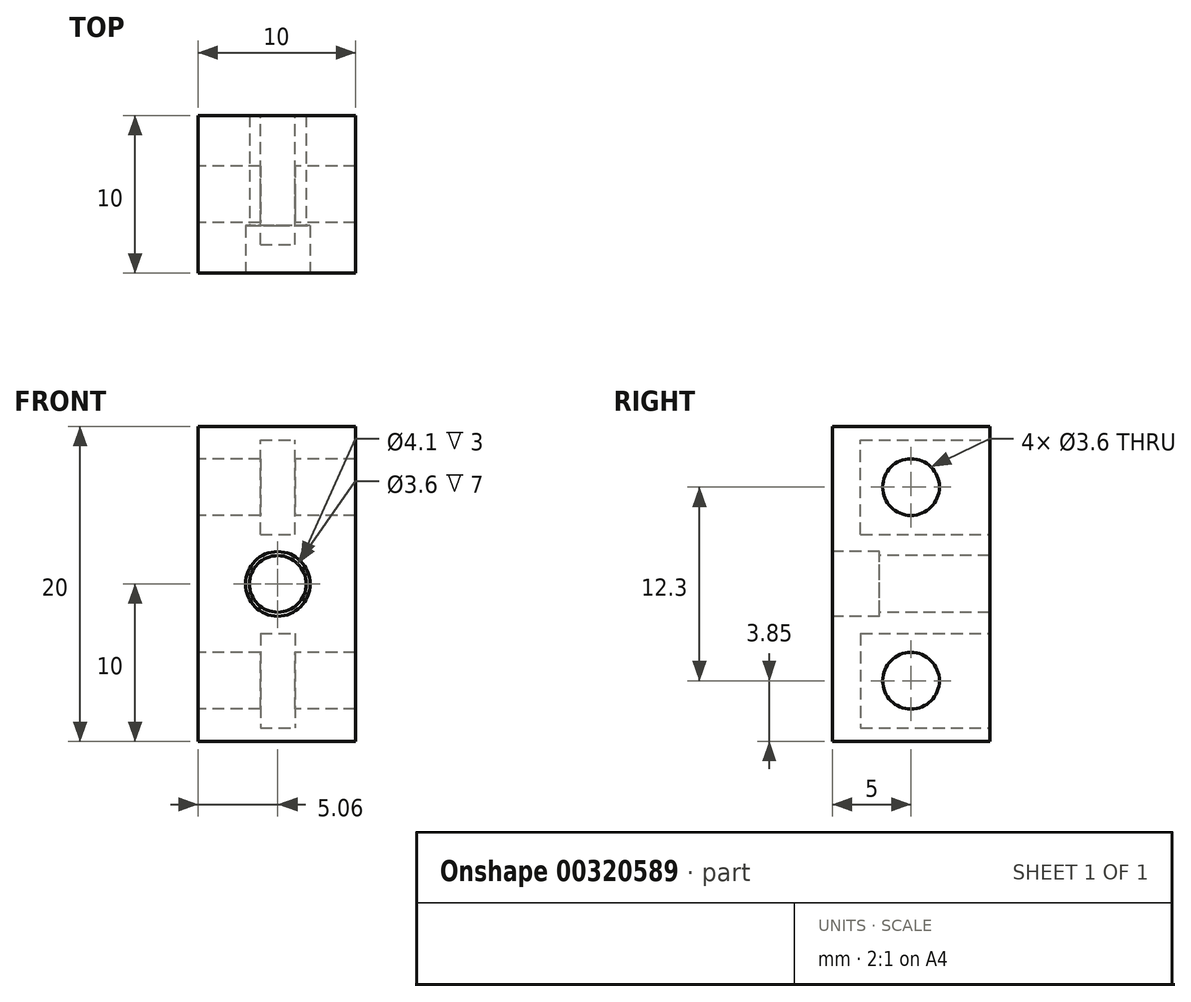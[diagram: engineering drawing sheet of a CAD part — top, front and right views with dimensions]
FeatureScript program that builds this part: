
annotation { "Feature Type Name" : "Feature", "Feature Type Description" : "" }
export const myFeature = defineFeature(function(context is Context, id is Id, definition is map)
    precondition{}
    {
        {
            var Q0;
            Q0=qCreatedBy(makeId("Front.planeOp"),FACE);
            var sketch = newSketch(context, id + "F0", { "sketchPlane" : qUnion([Q0])});
            skLineSegment(sketch, "E0.bottom", {"start": v(-5.06, 10) * mm, "end": v(4.94, 10) * mm});
            skLineSegment(sketch, "E0.top", {"start": v(-5.06, -10) * mm, "end": v(4.94, -10) * mm});
            skLineSegment(sketch, "E0.left", {"start": v(-5.06, 10) * mm, "end": v(-5.06, -10) * mm});
            skLineSegment(sketch, "E0.right", {"start": v(4.94, 10) * mm, "end": v(4.94, -10) * mm});
            skPoint(sketch, "E1", {"position": v(0, 0) * mm});
            skPoint(sketch, "E1.positionSnap0", {"position": v(4.94, 0) * mm});
            skCircle(sketch, "E2", {"center": v(0, 0) * mm, "radius": 3.25 * mm, "construction": true});
            skCircle(sketch, "E3", {"center": v(0, 0) * mm, "radius": 1.8 * mm, "construction": true});
            skLineSegment(sketch, "E4.bottom", {"start": v(-1.1, -3.15) * mm, "end": v(1.1, -3.15) * mm, "construction": true});
            skLineSegment(sketch, "E4.top", {"start": v(-1.1, -9.15) * mm, "end": v(1.1, -9.15) * mm, "construction": true});
            skLineSegment(sketch, "E4.left", {"start": v(-1.1, -3.15) * mm, "end": v(-1.1, -9.15) * mm, "construction": true});
            skLineSegment(sketch, "E4.right", {"start": v(1.1, -3.15) * mm, "end": v(1.1, -9.15) * mm, "construction": true});
            skPoint(sketch, "E5", {"position": v(1.1, -6.15) * mm});
            skPoint(sketch, "E6", {"position": v(0, -9.15) * mm});
            skLineSegment(sketch, "E7.MirrorCS", {"start": v(-1.1, 3.15) * mm, "end": v(-1.1, 9.15) * mm, "construction": true});
            skLineSegment(sketch, "E8.MirrorCS", {"start": v(-1.1, 3.15) * mm, "end": v(1.1, 3.15) * mm, "construction": true});
            skLineSegment(sketch, "E9.MirrorCS", {"start": v(1.1, 3.15) * mm, "end": v(1.1, 9.15) * mm, "construction": true});
            skLineSegment(sketch, "E10.MirrorCS", {"start": v(-1.1, 9.15) * mm, "end": v(1.1, 9.15) * mm, "construction": true});
            skLineSegment(sketch, "E11.MirrorCS", {"start": v(-1.1, 3.15) * mm, "end": v(-1.1, 9.15) * mm});
            skLineSegment(sketch, "E12.MirrorCS", {"start": v(-1.1, 3.15) * mm, "end": v(1.1, 3.15) * mm});
            skPoint(sketch, "E13.orphan", {"position": v(1.1, 2.85) * mm});
            skPoint(sketch, "E14.MirrorCS.start.orphan", {"position": v(1.1, -3.15) * mm});
            skSolve(sketch);
        }
        {
            var Q0;
            Q0=makeQuery(id+"F0.imprint","IMPRINT",FACE,{"disambiguationData":[TD([[makeQuery(id+"F0.imprint","IMPRINT",EDGE,{"derivedFrom":sQuery(id+"F0.wireOp",EDGE,"E0.bottom")}),-1.0]])]});
            extrude(context, id + "F1", {"entities" : qUnion([Q0]), "depth" : 10 * mm});
        }
        {
            var Q0;
            Q0=makeQuery(id+"F1.opExtrude","CAP_FACE",FACE,{"disambiguationData":[OSD([sQuery(id+"F0.wireOp",EDGE,"E0.bottom"),sQuery(id+"F0.wireOp",EDGE,"E0.top"),sQuery(id+"F0.wireOp",EDGE,"E0.left"),sQuery(id+"F0.wireOp",EDGE,"E0.right")])],"isStart":true});
            var sketch = newSketch(context, id + "F2", { "sketchPlane" : qUnion([Q0])});
            skLineSegment(sketch, "E15.0", {"start": v(1.1, 9.15) * mm, "end": v(-1.1, 9.15) * mm});
            skLineSegment(sketch, "E15.1", {"start": v(-1.1, 3.15) * mm, "end": v(-1.1, 9.15) * mm});
            skLineSegment(sketch, "E15.2", {"start": v(1.1, 3.15) * mm, "end": v(1.1, 9.15) * mm});
            skLineSegment(sketch, "E15.3", {"start": v(1.1, 3.15) * mm, "end": v(-1.1, 3.15) * mm});
            skLineSegment(sketch, "E15.4", {"start": v(1.1, -3.15) * mm, "end": v(-1.1, -3.15) * mm});
            skLineSegment(sketch, "E15.5", {"start": v(-1.1, -3.15) * mm, "end": v(-1.1, -9.15) * mm});
            skLineSegment(sketch, "E15.6", {"start": v(1.1, -3.15) * mm, "end": v(1.1, -9.15) * mm});
            skLineSegment(sketch, "E15.7", {"start": v(1.1, -9.15) * mm, "end": v(-1.1, -9.15) * mm});
            skSolve(sketch);
        }
        {
            var Q0;
            Q0 = qSketchRegion(id + "F2", true);
            extrude(context, id + "F3", {"entities" : qUnion([Q0]), "operationType" : NewBodyOperationType.REMOVE, "oppositeDirection" : true, "depth" : 8.2 * mm});
        }
        {
            var Q0;
            Q0=makeQuery(id+"F1.opExtrude","CAP_FACE",FACE,{"disambiguationData":[OSD([sQuery(id+"F0.wireOp",EDGE,"E0.bottom"),sQuery(id+"F0.wireOp",EDGE,"E0.top"),sQuery(id+"F0.wireOp",EDGE,"E0.left"),sQuery(id+"F0.wireOp",EDGE,"E0.right")])],"isStart":false});
            var sketch = newSketch(context, id + "F4", { "sketchPlane" : qUnion([Q0])});
            skCircle(sketch, "E16", {"center": v(0, 0) * mm, "radius": 2.05 * mm});
            skSolve(sketch);
        }
        {
            var Q0;
            Q0=makeQuery(id+"F4.imprint","IMPRINT",FACE,{"disambiguationData":[TD([[makeQuery(id+"F4.imprint","IMPRINT",EDGE,{"derivedFrom":sQuery(id+"F4.wireOp",EDGE,"E16")}),1.0]])]});
            var Q1;
            Q1=sQuery(id+"F4.wireOp",EDGE,"9281c9e8-2991-4c77-bb7b-1509dd7ab29b.0");
            extrude(context, id + "F5", {"entities" : qUnion([Q0]), "operationType" : NewBodyOperationType.REMOVE, "surfaceEntities" : qUnion([Q1]), "oppositeDirection" : true, "depth" : 3 * mm});
        }
        {
            var Q0;
            Q0=sQuery(id+"F0.wireOp",VERTEX,"E3.center");
            var Q1;
            Q1=makeQuery(id+"F1.opExtrude","SWEPT_BODY",BODY,{"disambiguationData":[OSD([sQuery(id+"F0.wireOp",EDGE,"E0.bottom"),sQuery(id+"F0.wireOp",EDGE,"E0.top"),sQuery(id+"F0.wireOp",EDGE,"E0.left"),sQuery(id+"F0.wireOp",EDGE,"E0.right")])]});
            hole(context, id + "F6", {"style" : HoleStyle.SIMPLE, "endStyle" : HoleEndStyle.THROUGH, "oppositeDirection" : true, "holeDiameter" : 3.6 * mm, "tappedDepth" : 12 * mm, "tapClearance" : 3, "locations" : qUnion([Q0]), "scope" : qUnion([Q1])});
        }
        {
            var Q0;
            Q0=makeQuery(id+"F1.opExtrude","SWEPT_FACE",FACE,{"disambiguationData":[OSD([sQuery(id+"F0.wireOp",EDGE,"E0.right")])]});
            var sketch = newSketch(context, id + "F7", { "sketchPlane" : qUnion([Q0])});
            skLineSegment(sketch, "E17.bottom", {"start": v(-5, -10) * mm, "end": v(-5, -10) * mm});
            skLineSegment(sketch, "E17.top", {"start": v(-5, 10) * mm, "end": v(-5, 10) * mm});
            skLineSegment(sketch, "E17.left", {"start": v(-5, -10) * mm, "end": v(-5, 10) * mm});
            skLineSegment(sketch, "E17.right", {"start": v(-5, -10) * mm, "end": v(-5, 10) * mm, "construction": true});
            skLineSegment(sketch, "E18.bottom", {"start": v(-10, 0) * mm, "end": v(0, 0) * mm, "construction": true});
            skLineSegment(sketch, "E18.top", {"start": v(-10, 0) * mm, "end": v(0, 0) * mm, "construction": true});
            skLineSegment(sketch, "E18.left", {"start": v(-10, 0) * mm, "end": v(-10, 0) * mm});
            skLineSegment(sketch, "E18.right", {"start": v(0, 0) * mm, "end": v(0, 0) * mm});
            skPoint(sketch, "E19.0", {"position": v(0, -6.15) * mm});
            skPoint(sketch, "E19.1", {"position": v(0, 6.15) * mm});
            skLineSegment(sketch, "E20", {"start": v(0, -6.15) * mm, "end": v(-10, -6.15) * mm, "construction": true});
            skLineSegment(sketch, "E21", {"start": v(0, 6.15) * mm, "end": v(-10, 6.15) * mm, "construction": true});
            skPoint(sketch, "E22", {"position": v(-5, -6.15) * mm});
            skPoint(sketch, "E23", {"position": v(-5, 6.15) * mm});
            skSolve(sketch);
        }
        {
            var Q0;
            Q0=sQuery(id+"F7.wireOp",VERTEX,"E22");
            var Q1;
            Q1=sQuery(id+"F7.wireOp",VERTEX,"E23");
            var Q2;
            Q2=makeQuery(id+"F1.opExtrude","SWEPT_BODY",BODY,{"disambiguationData":[OSD([sQuery(id+"F0.wireOp",EDGE,"E0.bottom"),sQuery(id+"F0.wireOp",EDGE,"E0.top"),sQuery(id+"F0.wireOp",EDGE,"E0.left"),sQuery(id+"F0.wireOp",EDGE,"E0.right")])]});
            hole(context, id + "F8", {"style" : HoleStyle.SIMPLE, "endStyle" : HoleEndStyle.THROUGH, "holeDiameter" : 3.6 * mm, "tappedDepth" : 12 * mm, "tapClearance" : 3, "locations" : qUnion([Q0, Q1]), "scope" : qUnion([Q2])});
        }
    });
